# Revit family: LAMP_HANCE DOWNLIGHT RECESSED MEDIUM FLOOD 1000_2000
name_source: partatom
category: Modelos genéricos
revit_build: Autodesk Revit 2015 (Build: 20140606_1530(x64)
units: mm (PartAtom-declared; Revit-internal decimal feet)

## types (8) — shared parameters
CRI = 80
Comentarios de tipo = Availability of tilting between 0º and 30º when placed in a project.
Diameter = 143 mm
Elevación por defecto = 1219 mm
Fabricante = LAMP
Gear = Electronic
IEE = A+
Installation instructions = https://www.lamp.es
Insulation class = II
Lamp = COB LED
Last update = 18/10/2019
Luminaire type = Indoor - Recessed downlight
MacAdam = 3
Manufacturer URL = http://www.lamp.es
Manufacturer country = Spain
Manufacturer name = LAMP
Material interior aro = LAMP_Aluminio Hance Negro
Model explanation = Availability of tilting between 0º and 30º when placed in a project.
Power Supply = 220-240V 50/60Hz
Product URL = https://www.lamp.es
Product datasheet = http://www.lamp.es
Protection rating = IP20
Recessed diameter = 132 mm  [stored 0.433071 ft]
Type = COB PHILIPS
Weight = 0.72 kg

## per-type parameters (varying)
| type | Descripción | Efficacy | Finish | Initial color | Initial intensity | LED Lifetime | Material aro | Modelo | Photometric web file | Plum | Power | Product code |
| 740LM 4000K 1000 BLACK | HANCE DOWN REC 1000 NW MFL BK. | 97 lm/W | Texturised black RAL 9011 | 4000 K | 740 lm | 50.000 L90 B10 | LAMP_Aluminio Hance Negro | HD1RE10MF840NBB | Cuerpo Hance BASE (tilting)_MF : 740LM 4000K 1000 BLACK | 8 W | 7 W | HD1RE10MF840NBB |
| 740LM 4000K 1000 WHITE | HANCE DOWN REC 1000 NW MFL WH. | 97 lm/W | Texturised white RAL 9010 | 4000 K | 740 lm | 50.000 L90 B10 | LAMP_Aluminio Hance Blanco | HD1RE10MF840NBW | Cuerpo Hance BASE (tilting)_MF : 740LM 4000K 1000 WHITE | 8 W | 7 W | HD1RE10MF840NBW |
| 806LM 3000K 1000 BLACK | HANCE DOWN REC 1000 WW MFL BK. | 105 lm/W | Texturised black RAL 9011 | 3000 K | 806 lm | 50.000 L90 B10 | LAMP_Aluminio Hance Negro | HD1RE10MF830NBB | Cuerpo Hance BASE (tilting)_MF : 806LM 3000K 1000 BLACK | 8 W | 7 W | HD1RE10MF830NBB |
| 806LM 3000K 1000 WHITE | HANCE DOWN REC 1000 WW MFL WH. | 105 lm/W | Texturised white RAL 9010 | 3000 K | 806 lm | 50.000 L90 B10 | LAMP_Aluminio Hance Blanco | HD1RE10MF830NBW | Cuerpo Hance BASE (tilting)_MF : 806LM 3000K 1000 WHITE | 8 W | 7 W | HD1RE10MF830NBW |
| 1606LM 4000K 2000 BLACK | HANCE DOWN REC 2000 NW MFL BK. | 78 lm/W | Texturised black RAL 9011 | 4000 K | 1606 lm | 50.000 L80 B10 | LAMP_Aluminio Hance Negro | HD1RE20MF840NBB | Cuerpo Hance BASE (tilting)_MF : 1606LM 4000K 2000 BLACK | 21 W | 18 W | HD1RE20MF840NBB |
| 1606LM 4000K 2000 WHITE | HANCE DOWN REC 2000 NW MFL WH. | 78 lm/W | Texturised white RAL 9010 | 4000 K | 1606 lm | 50.000 L80 B10 | LAMP_Aluminio Hance Blanco | HD1RE20MF840NBW | Cuerpo Hance BASE (tilting)_MF : 1606LM 4000K 2000 WHITE | 21 W | 18 W | HD1RE20MF840NBW |
| 1760LM 3000K 2000 BLACK | HANCE DOWN REC 2000 WW MFL BK. | 85 lm/W | Texturised black RAL 9011 | 3000 K | 1760 lm | 50.000 L80 B10 | LAMP_Aluminio Hance Negro | HD1RE20MF830NBB | Cuerpo Hance BASE (tilting)_MF : 1760LM 3000K 2000 BLACK | 21 W | 18 W | HD1RE20MF830NBB |
| 1760LM 3000K 2000 WHITE | HANCE DOWN REC 2000 WW MFL WH. | 85 lm/W | Texturised white RAL 9010 | 3000 K | 1760 lm | 50.000 L80 B10 | LAMP_Aluminio Hance Blanco | HD1RE20MF830NBW | Cuerpo Hance BASE (tilting)_MF : 1760LM 3000K 2000 WHITE | 21 W | 18 W | HD1RE20MF830NBW |

note: [stored X ft] marks values corroborated as IEEE doubles in the binary element streams (Revit-internal decimal feet)
